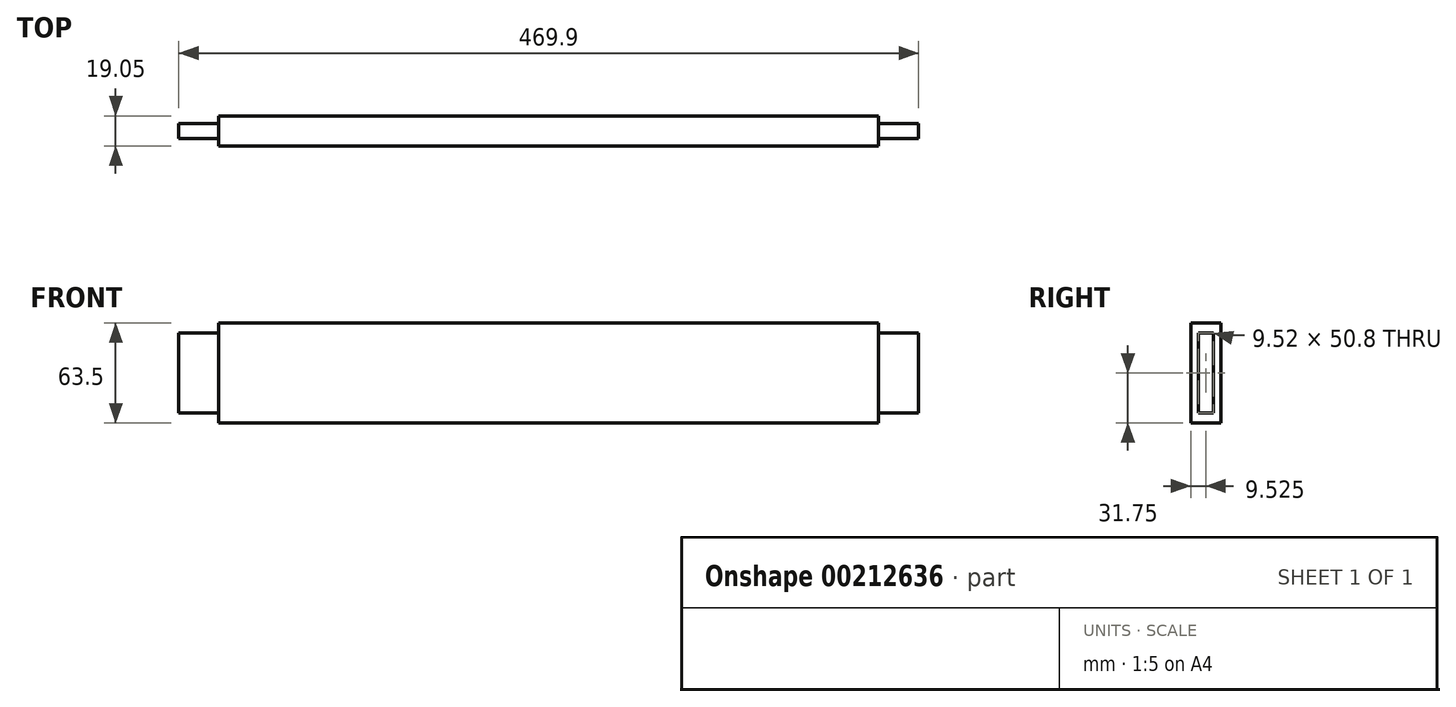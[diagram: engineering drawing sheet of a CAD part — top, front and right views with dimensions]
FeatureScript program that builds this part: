
annotation { "Feature Type Name" : "Feature", "Feature Type Description" : "" }
export const myFeature = defineFeature(function(context is Context, id is Id, definition is map)
    precondition{}
    {
        {
            var Q0;
            Q0=qCreatedBy(makeId("Front.planeOp"),FACE);
            var sketch = newSketch(context, id + "F0", { "sketchPlane" : qUnion([Q0])});
            skLineSegment(sketch, "E0.bottom", {"start": v(-209.55, 0) * mm, "end": v(209.55, 0) * mm});
            skLineSegment(sketch, "E0.top", {"start": v(-209.55, -63.5) * mm, "end": v(209.55, -63.5) * mm});
            skLineSegment(sketch, "E0.left", {"start": v(-209.55, 0) * mm, "end": v(-209.55, -63.5) * mm});
            skLineSegment(sketch, "E0.right", {"start": v(209.55, 0) * mm, "end": v(209.55, -63.5) * mm});
            skSolve(sketch);
        }
        {
            var Q0;
            Q0=makeQuery(id+"F0.imprint","IMPRINT",FACE,{"disambiguationData":[TD([[makeQuery(id+"F0.imprint","IMPRINT",EDGE,{"derivedFrom":sQuery(id+"F0.wireOp",EDGE,"E0.bottom")}),-1.0]])]});
            extrude(context, id + "F1", {"entities" : qUnion([Q0]), "depth" : 19.05 * mm});
        }
        {
            var Q0;
            Q0=makeQuery(id+"F1.opExtrude","SWEPT_FACE",FACE,{"disambiguationData":[OSD([sQuery(id+"F0.wireOp",EDGE,"E0.right")])]});
            var sketch = newSketch(context, id + "F2", { "sketchPlane" : qUnion([Q0])});
            skLineSegment(sketch, "E1.bottom", {"start": v(-14.29, -6.35) * mm, "end": v(-14.29, -57.15) * mm});
            skLineSegment(sketch, "E1.top", {"start": v(-4.76, -6.35) * mm, "end": v(-4.76, -57.15) * mm});
            skLineSegment(sketch, "E1.left", {"start": v(-14.29, -6.35) * mm, "end": v(-4.76, -6.35) * mm});
            skLineSegment(sketch, "E1.right", {"start": v(-14.29, -57.15) * mm, "end": v(-4.76, -57.15) * mm});
            skSolve(sketch);
        }
        {
            var Q0;
            Q0=makeQuery(id+"F2.imprint","IMPRINT",FACE,{"disambiguationData":[TD([[makeQuery(id+"F2.imprint","IMPRINT",EDGE,{"derivedFrom":sQuery(id+"F2.wireOp",EDGE,"E1.bottom")}),1.0]])]});
            extrude(context, id + "F3", {"entities" : qUnion([Q0]), "operationType" : NewBodyOperationType.ADD, "depth" : 25.4 * mm});
        }
        {
            var Q0;
            Q0=makeQuery(id+"F1.opExtrude","SWEPT_FACE",FACE,{"disambiguationData":[OSD([sQuery(id+"F0.wireOp",EDGE,"E0.left")])]});
            var sketch = newSketch(context, id + "F4", { "sketchPlane" : qUnion([Q0])});
            skLineSegment(sketch, "E2.bottom", {"start": v(4.76, -6.35) * mm, "end": v(4.76, -57.15) * mm});
            skLineSegment(sketch, "E2.top", {"start": v(14.29, -6.35) * mm, "end": v(14.29, -57.15) * mm});
            skLineSegment(sketch, "E2.left", {"start": v(4.76, -6.35) * mm, "end": v(14.29, -6.35) * mm});
            skLineSegment(sketch, "E2.right", {"start": v(4.76, -57.15) * mm, "end": v(14.29, -57.15) * mm});
            skSolve(sketch);
        }
        {
            var Q0;
            Q0=makeQuery(id+"F4.imprint","IMPRINT",FACE,{"disambiguationData":[TD([[makeQuery(id+"F4.imprint","IMPRINT",EDGE,{"derivedFrom":sQuery(id+"F4.wireOp",EDGE,"E2.bottom")}),1.0]])]});
            extrude(context, id + "F5", {"entities" : qUnion([Q0]), "operationType" : NewBodyOperationType.ADD, "depth" : 25.4 * mm});
        }
    });
